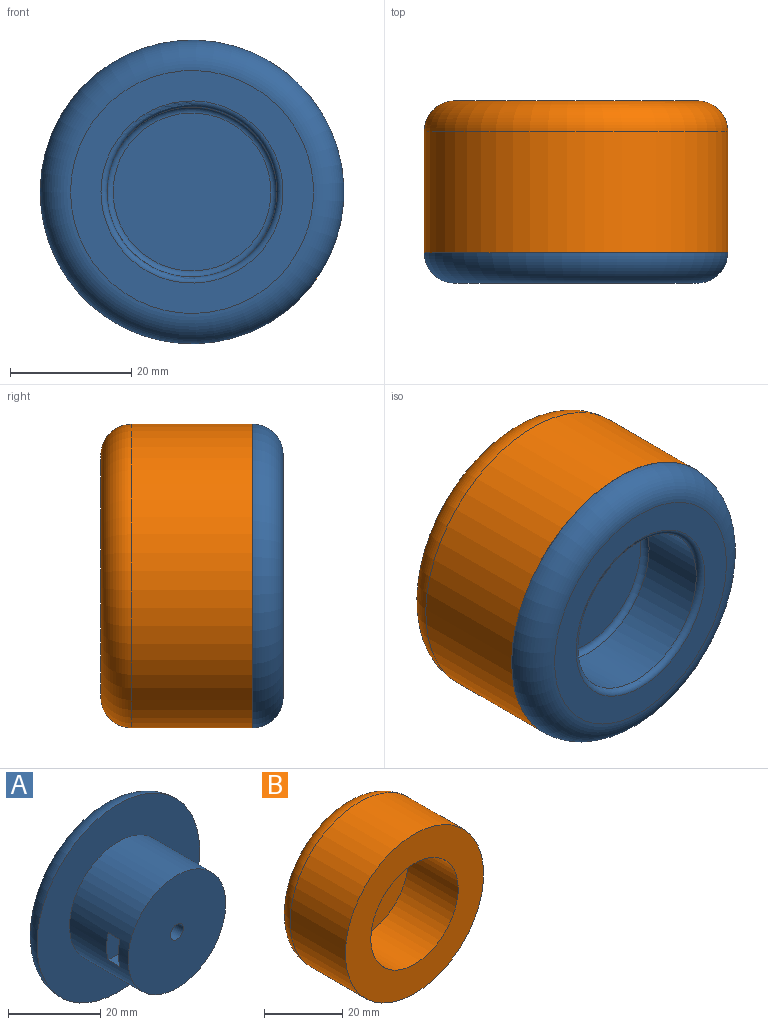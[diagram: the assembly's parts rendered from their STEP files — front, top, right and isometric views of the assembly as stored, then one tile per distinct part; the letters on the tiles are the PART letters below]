
ASSEMBLY  parts=2 mates=1
PART A: 15 faces, bbox 54.1x23x54.1 mm
  f0: cylinder r=2mm len=4mm, axis (0,-1,0), area 37.6mm2, adj f2,f13
  f1: cylinder r=15mm len=30mm, axis (0,1,0), area 1670.3mm2, adj f2,f3,f10,f11,f12,f13
  f2: plane 30x30mm, normal (0,-1,0), area 694.3mm2, adj f0,f1
  f3: plane 50x50mm, normal (0,-1,0), area 1256.6mm2, adj f1,f5
  f4: plane 40x40mm, normal (0,1,0), area 549.8mm2, adj f5,f8
  f5: torus R=20mm, axis (0,-1,0), area 1144mm2, adj f3,f4
  f6: cylinder r=14mm len=28mm, axis (0,1,0), area 967.6mm2, adj f8,f9
  f7: plane 26x26mm, normal (0,1,0), area 530.9mm2, adj f9
  f8: torus R=15mm, axis (0,-1,0), area 141.8mm2, adj f4,f6
  f9: torus R=13mm, axis (0,1,0), area 134.6mm2, adj f6,f7
  f10: plane 18.31x3.6mm, normal (0,0,-1), area 65.9mm2, adj f1,f12,f13,f14
  f11: plane 18.37x3.6mm, normal (0,0,1), area 66.1mm2, adj f1,f12,f13,f14
  f12: plane 18.78x7.2mm, normal (0,-1,0), area 134.1mm2, adj f1,f10,f11,f14
  f13: plane 18.78x7.2mm, normal (0,1,0), area 121.6mm2, adj f0,f1,f10,f11,f14
  f14: plane 7.2x3.6mm, normal (-1,0,0), area 25.9mm2, adj f10,f11,f12,f13
PART B: 9 faces, bbox 54.1x25x54.1 mm
  f0: cylinder r=2mm len=5mm, axis (0,1,0), area 62.8mm2, adj f5,f8
  f1: cylinder r=25mm len=50mm, axis (0,-1,0), area 3141.6mm2, adj f3,f4
  f2: plane 40x40mm, normal (0,1,0), area 1206.4mm2, adj f4,f6
  f3: plane 50x50mm, normal (0,-1,0), area 1179.2mm2, adj f1,f7
  f4: torus R=20mm, axis (0,-1,0), area 1144mm2, adj f1,f2
  f5: plane 8x8mm, normal (0,1,0), area 37.7mm2, adj f0,f6
  f6: cylinder r=4mm len=8mm, axis (0,1,0), area 50.3mm2, adj f2,f5
  f7: cylinder r=15.8mm len=31.6mm, axis (0,-1,0), area 1786.9mm2, adj f3,f8
  f8: plane 31.6x31.6mm, normal (0,-1,0), area 771.7mm2, adj f0,f7
PLACE A rot(axis=(0.71,0,0.71),180deg) t=(2.02,-15.89,2.92)mm
PLACE B t=(2.02,-15.89,2.92)mm
MATE cylindrical B.f0 <-> A.f0  axis (0,-1,0) through (2.02,2.11,2.92)mm
